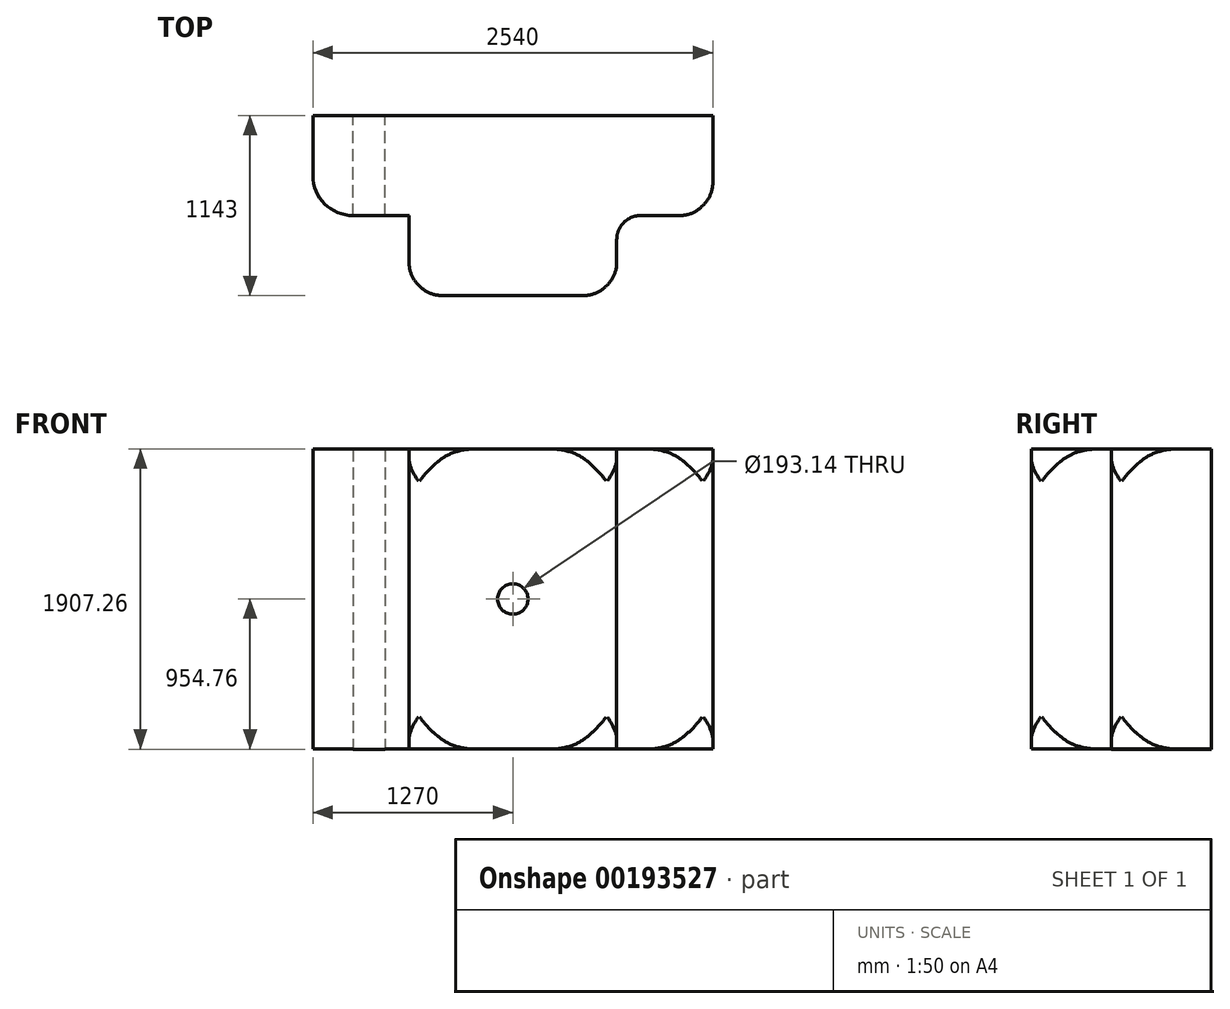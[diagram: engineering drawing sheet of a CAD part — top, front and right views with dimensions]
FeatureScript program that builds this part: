
annotation { "Feature Type Name" : "Feature", "Feature Type Description" : "" }
export const myFeature = defineFeature(function(context is Context, id is Id, definition is map)
    precondition{}
    {
        {
            var Q0;
            Q0=qCreatedBy(makeId("Front.planeOp"),FACE);
            var sketch = newSketch(context, id + "F0", { "sketchPlane" : qUnion([Q0])});
            skLineSegment(sketch, "E0.bottom", {"start": v(1270, 952.5) * mm, "end": v(-1270, 952.5) * mm});
            skLineSegment(sketch, "E0.top", {"start": v(1270, -952.5) * mm, "end": v(-1270, -952.5) * mm});
            skLineSegment(sketch, "E0.left", {"start": v(1270, 952.5) * mm, "end": v(1270, -952.5) * mm});
            skLineSegment(sketch, "E0.right", {"start": v(-1270, 952.5) * mm, "end": v(-1270, -952.5) * mm});
            skPoint(sketch, "E0.middle", {"position": v(0, 0) * mm});
            skSolve(sketch);
        }
        {
            var Q0;
            Q0 = qSketchRegion(id + "F0", true);
            extrude(context, id + "F1", {"entities" : qUnion([Q0]), "depth" : 635 * mm});
        }
        {
            var Q0;
            Q0=makeQuery(id+"F1.opExtrude","CAP_FACE",FACE,{"disambiguationData":[OSD([sQuery(id+"F0.wireOp",EDGE,"E0.bottom"),sQuery(id+"F0.wireOp",EDGE,"E0.top"),sQuery(id+"F0.wireOp",EDGE,"E0.left"),sQuery(id+"F0.wireOp",EDGE,"E0.right")])],"isStart":false});
            var sketch = newSketch(context, id + "F2", { "sketchPlane" : qUnion([Q0])});
            skLineSegment(sketch, "E1.bottom", {"start": v(659.62, 952.5) * mm, "end": v(-659.62, 952.5) * mm});
            skLineSegment(sketch, "E1.top", {"start": v(659.62, -952.5) * mm, "end": v(-659.62, -952.5) * mm});
            skLineSegment(sketch, "E1.left", {"start": v(659.62, 952.5) * mm, "end": v(659.62, -952.5) * mm});
            skLineSegment(sketch, "E1.right", {"start": v(-659.62, 952.5) * mm, "end": v(-659.62, -952.5) * mm});
            skPoint(sketch, "E1.middle", {"position": v(0, 0) * mm});
            skSolve(sketch);
        }
        {
            var Q0;
            Q0=makeQuery(id+"F2.imprint","IMPRINT",FACE,{"disambiguationData":[TD([[makeQuery(id+"F2.imprint","IMPRINT",EDGE,{"derivedFrom":sQuery(id+"F2.wireOp",EDGE,"E1.bottom")}),1.0]])]});
            var sketch = newSketch(context, id + "F3", { "sketchPlane" : qUnion([Q0])});
            skSolve(sketch);
        }
        {
            var Q0;
            Q0=makeQuery(id+"F2.imprint","IMPRINT",FACE,{"disambiguationData":[TD([[makeQuery(id+"F2.imprint","IMPRINT",EDGE,{"derivedFrom":sQuery(id+"F2.wireOp",EDGE,"E1.bottom")}),1.0]])]});
            extrude(context, id + "F4", {"entities" : qUnion([Q0]), "operationType" : NewBodyOperationType.ADD, "depth" : 508 * mm});
        }
        {
            var Q0;
            Q0=makeQuery(id+"F4.opExtrude","CAP_EDGE",EDGE,{"disambiguationData":[OSD([sQuery(id+"F2.wireOp",EDGE,"E1.right")])],"isStart":true});
            var Q1;
            Q1=makeQuery(id+"F4.opExtrude","CAP_EDGE",EDGE,{"disambiguationData":[OSD([sQuery(id+"F2.wireOp",EDGE,"E1.left")])],"isStart":true});
            fillet(context, id + "F5", {"entities" : qUnion([Q0, Q1]), "radius" : 152.4 * mm, "tangentPropagation" : true, "allowEdgeOverflow" : false});
        }
        {
            var Q0;
            Q0=makeQuery(id+"F4.opExtrude","CAP_EDGE",EDGE,{"disambiguationData":[OSD([sQuery(id+"F2.wireOp",EDGE,"E1.left")])],"isStart":false});
            var Q1;
            Q1=makeQuery(id+"F4.opExtrude","CAP_EDGE",EDGE,{"disambiguationData":[OSD([sQuery(id+"F2.wireOp",EDGE,"E1.right")])],"isStart":false});
            var Q2;
            Q2=makeQuery(id+"F1.opExtrude","CAP_EDGE",EDGE,{"disambiguationData":[OSD([sQuery(id+"F0.wireOp",EDGE,"E0.left")])],"isStart":false});
            chamfer(context, id + "F6", {"entities" : qUnion([Q0, Q1, Q2]), "width" : 127 * mm, "tangentPropagation" : true});
        }
        {
            var Q0;
            Q0=makeQuery(id+"F6.opChamfer","BLEND_FACE",FACE,{"disambiguationData":[OSD([sQuery(id+"F0.wireOp",EDGE,"E0.left")])]});
            var Q1;
            Q1=makeQuery(id+"F6.opChamfer","BLEND_FACE",FACE,{"disambiguationData":[OSD([sQuery(id+"F2.wireOp",EDGE,"E1.left")])]});
            var Q2;
            Q2=makeQuery(id+"F6.opChamfer","BLEND_FACE",FACE,{"disambiguationData":[OSD([sQuery(id+"F2.wireOp",EDGE,"E1.right")])]});
            fillet(context, id + "F7", {"entities" : qUnion([Q0, Q1, Q2]), "radius" : 203.2 * mm, "tangentPropagation" : true, "allowEdgeOverflow" : false});
        }
        {
            var Q0;
            Q0=makeQuery(id+"F1.opExtrude","CAP_EDGE",EDGE,{"disambiguationData":[OSD([sQuery(id+"F0.wireOp",EDGE,"E0.right")])],"isStart":false});
            fillet(context, id + "F8", {"entities" : qUnion([Q0]), "radius" : 254 * mm, "tangentPropagation" : true, "allowEdgeOverflow" : false});
        }
        {
            var Q0;
            Q0=makeQuery(id+"F1.opExtrude","CAP_FACE",FACE,{"disambiguationData":[OSD([sQuery(id+"F0.wireOp",EDGE,"E0.bottom"),sQuery(id+"F0.wireOp",EDGE,"E0.top"),sQuery(id+"F0.wireOp",EDGE,"E0.left"),sQuery(id+"F0.wireOp",EDGE,"E0.right")])],"isStart":true});
            shell(context, id + "F9", {"entities" : qUnion([Q0]), "thickness" : 2.54 * mm});
        }
        {
            var Q0;
            Q0=makeQuery(id+"F4.opExtrude","CAP_FACE",FACE,{"disambiguationData":[OSD([sQuery(id+"F2.wireOp",EDGE,"E1.bottom"),sQuery(id+"F2.wireOp",EDGE,"E1.top"),sQuery(id+"F2.wireOp",EDGE,"E1.left"),sQuery(id+"F2.wireOp",EDGE,"E1.right")])],"isStart":false});
            var sketch = newSketch(context, id + "F10", { "sketchPlane" : qUnion([Q0])});
            skCircle(sketch, "E2", {"center": v(0, 0) * mm, "radius": 96.57 * mm});
            skSolve(sketch);
        }
        {
            var Q0;
            Q0 = qSketchRegion(id + "F10", true);
            extrude(context, id + "F11", {"entities" : qUnion([Q0]), "operationType" : NewBodyOperationType.REMOVE, "oppositeDirection" : true, "depth" : 254 * mm, "offsetDistance" : 25.4 * mm});
        }
        {
            var Q0;
            Q0=makeQuery(id+"F3.imprint","IMPRINT",FACE,{"disambiguationData":[TD([[makeQuery(id+"F3.imprint","IMPRINT",EDGE,{"derivedFrom":makeQuery(id+"F2.imprint","IMPRINT",EDGE,{"derivedFrom":sQuery(id+"F2.wireOp",EDGE,"E1.bottom")})}),1.0]])]});
            var sketch = newSketch(context, id + "F12", { "sketchPlane" : qUnion([Q0])});
            skLineSegment(sketch, "E3.bottom", {"start": v(-1016.14, 950.65) * mm, "end": v(-811.5, 950.65) * mm});
            skLineSegment(sketch, "E3.top", {"start": v(-1016.14, -954.76) * mm, "end": v(-811.5, -954.76) * mm});
            skLineSegment(sketch, "E3.left", {"start": v(-1016.14, 950.65) * mm, "end": v(-1016.14, -954.76) * mm});
            skLineSegment(sketch, "E3.right", {"start": v(-811.5, 950.65) * mm, "end": v(-811.5, -954.76) * mm});
            skSolve(sketch);
        }
        {
            var Q0;
            Q0 = qSketchRegion(id + "F12", true);
            extrude(context, id + "F13", {"entities" : qUnion([Q0]), "operationType" : NewBodyOperationType.ADD, "oppositeDirection" : true, "depth" : 635 * mm, "offsetDistance" : 25.4 * mm});
        }
    });
